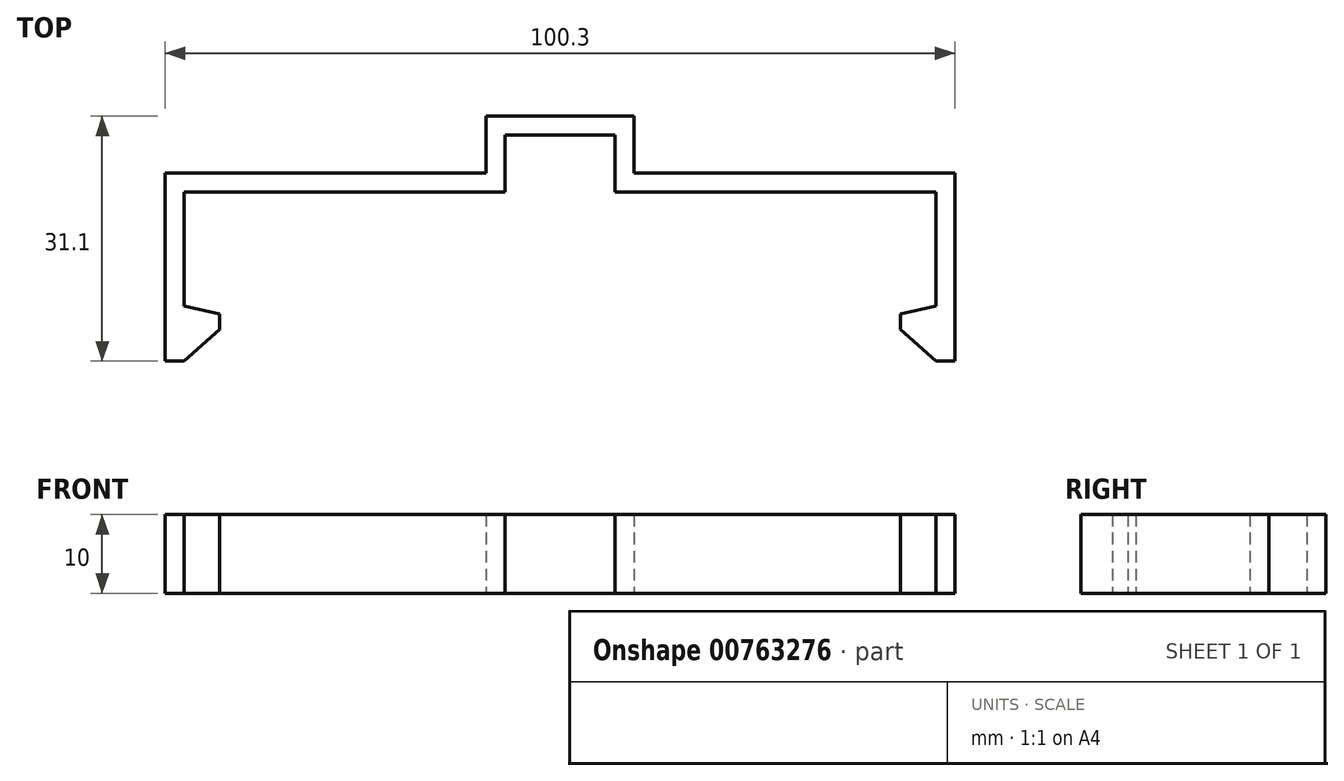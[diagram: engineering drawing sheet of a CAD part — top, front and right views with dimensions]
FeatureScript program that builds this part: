
annotation { "Feature Type Name" : "Feature", "Feature Type Description" : "" }
export const myFeature = defineFeature(function(context is Context, id is Id, definition is map)
    precondition{}
    {
        {
            assignVariable(context, id + "F0", {"name" : "clamp_width", "anyValue" : 10});
        }
        {
            var Q0;
            Q0=qCreatedBy(makeId("Top.planeOp"),FACE);
            var sketch = newSketch(context, id + "F1", { "sketchPlane" : qUnion([Q0])});
            skLineSegment(sketch, "E0", {"start": v(0, 7.2) * mm, "end": v(-7, 7.2) * mm});
            skLineSegment(sketch, "E1", {"start": v(-7, 7.2) * mm, "end": v(-7, 0) * mm});
            skLineSegment(sketch, "E2", {"start": v(-7, 0) * mm, "end": v(-47.75, 0) * mm});
            skLineSegment(sketch, "E3", {"start": v(-47.75, 0) * mm, "end": v(-47.75, -14.5) * mm});
            skLineSegment(sketch, "E4", {"start": v(-47.75, -14.5) * mm, "end": v(-43.25, -15.5) * mm});
            skLineSegment(sketch, "E5", {"start": v(-50.15, -21.5) * mm, "end": v(-50.15, 2.4) * mm});
            skLineSegment(sketch, "E6", {"start": v(-50.15, 2.4) * mm, "end": v(-9.4, 2.4) * mm});
            skLineSegment(sketch, "E7", {"start": v(-9.4, 2.4) * mm, "end": v(-9.4, 9.6) * mm});
            skLineSegment(sketch, "E8", {"start": v(-9.4, 9.6) * mm, "end": v(0, 9.6) * mm});
            skLineSegment(sketch, "E9", {"start": v(-50.15, -21.5) * mm, "end": v(-47.75, -21.5) * mm});
            skLineSegment(sketch, "E10", {"start": v(-47.75, -21.5) * mm, "end": v(-43.25, -17.5) * mm});
            skLineSegment(sketch, "E11", {"start": v(-43.25, -17.5) * mm, "end": v(-43.25, -15.5) * mm});
            skLineSegment(sketch, "E12", {"start": v(0, 9.6) * mm, "end": v(0, 7.2) * mm});
            skSolve(sketch);
        }
        {
            var Q0;
            Q0=makeQuery(id+"F1.imprint","IMPRINT",FACE,{"disambiguationData":[TD([[makeQuery(id+"F1.imprint","IMPRINT",EDGE,{"derivedFrom":sQuery(id+"F1.wireOp",EDGE,"E0")}),-1.0]])]});
            extrude(context, id + "F2", {"entities" : qUnion([Q0]), "depth" : (getVariable(context, 'clamp_width')) * mm, "offsetDistance" : 25 * mm});
        }
        {
            var Q0;
            Q0=makeQuery(id+"F2.opExtrude","SWEPT_BODY",BODY,{"disambiguationData":[OSD([sQuery(id+"F1.wireOp",EDGE,"E0"),sQuery(id+"F1.wireOp",EDGE,"E1"),sQuery(id+"F1.wireOp",EDGE,"E2"),sQuery(id+"F1.wireOp",EDGE,"E3"),sQuery(id+"F1.wireOp",EDGE,"E4"),sQuery(id+"F1.wireOp",EDGE,"E5"),sQuery(id+"F1.wireOp",EDGE,"E6"),sQuery(id+"F1.wireOp",EDGE,"E7"),sQuery(id+"F1.wireOp",EDGE,"E8"),sQuery(id+"F1.wireOp",EDGE,"E9"),sQuery(id+"F1.wireOp",EDGE,"E10"),sQuery(id+"F1.wireOp",EDGE,"E11"),sQuery(id+"F1.wireOp",EDGE,"E12")])]});
            var Q1;
            Q1=qCreatedBy(makeId("Right.planeOp"),FACE);
            mirror(context, id + "F3", {"operationType" : NewBodyOperationType.ADD, "entities" : qUnion([Q0]), "mirrorPlane" : qUnion([Q1])});
        }
    });
